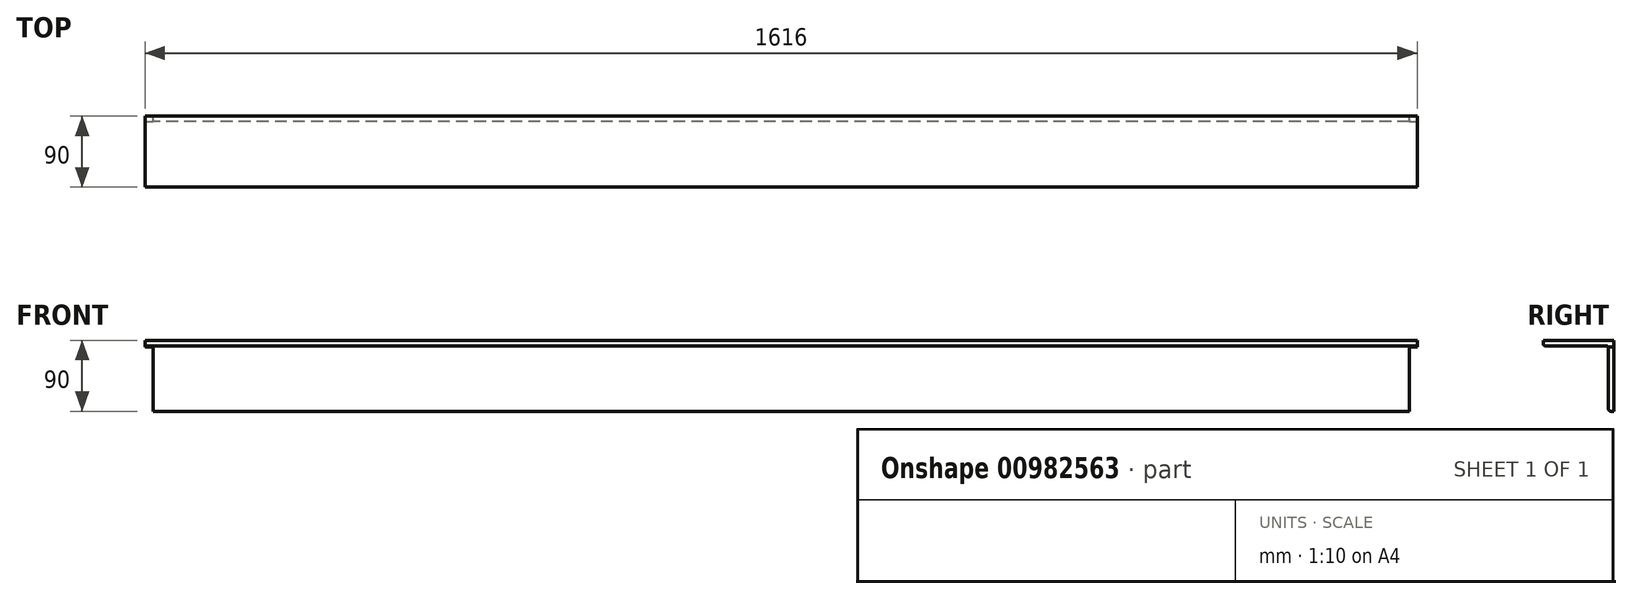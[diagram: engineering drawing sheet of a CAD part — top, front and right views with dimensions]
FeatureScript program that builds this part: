
annotation { "Feature Type Name" : "Feature", "Feature Type Description" : "" }
export const myFeature = defineFeature(function(context is Context, id is Id, definition is map)
    precondition{}
    {
        {
            var Q0;
            Q0=qCreatedBy(makeId("Right.planeOp"),FACE);
            var sketch = newSketch(context, id + "F0", { "sketchPlane" : qUnion([Q0])});
            skLineSegment(sketch, "E0", {"start": v(0, 0) * mm, "end": v(-90, 0) * mm});
            skLineSegment(sketch, "E1", {"start": v(-90, 0) * mm, "end": v(-90, -4) * mm});
            skLineSegment(sketch, "E2", {"start": v(-87, -7) * mm, "end": v(-10, -7) * mm});
            skLineSegment(sketch, "E3", {"start": v(-7, -10) * mm, "end": v(-7, -87) * mm});
            skLineSegment(sketch, "E4", {"start": v(-4, -90) * mm, "end": v(0, -90) * mm});
            skLineSegment(sketch, "E5", {"start": v(0, -90) * mm, "end": v(0, 0) * mm});
            skPoint(sketch, "E6.visualSharp", {"position": v(-90, -7) * mm});
            skArc(sketch, "E6.filletArc", {"start": v(-90, -4) * mm, "mid": v(-89.12, -6.12) * mm, "end": v(-87, -7) * mm});
            skPoint(sketch, "E7.visualSharp", {"position": v(-7, -7) * mm});
            skArc(sketch, "E7.filletArc", {"start": v(-7, -10) * mm, "mid": v(-7.88, -7.88) * mm, "end": v(-10, -7) * mm});
            skPoint(sketch, "E8.visualSharp", {"position": v(-7, -90) * mm});
            skArc(sketch, "E8.filletArc", {"start": v(-7, -87) * mm, "mid": v(-6.12, -89.12) * mm, "end": v(-4, -90) * mm});
            skSolve(sketch);
        }
        {
            var Q0;
            Q0=makeQuery(id+"F0.imprint","IMPRINT",FACE,{"disambiguationData":[TD([[makeQuery(id+"F0.imprint","IMPRINT",EDGE,{"derivedFrom":sQuery(id+"F0.wireOp",EDGE,"E0")}),1.0]])]});
            extrude(context, id + "F1", {"entities" : qUnion([Q0]), "endBound" : BoundingType.SYMMETRIC, "depth" : 1616 * mm, "offsetDistance" : 25 * mm});
        }
        {
            var Q0;
            Q0=makeQuery(id+"F1.opExtrude","SWEPT_FACE",FACE,{"disambiguationData":[OSD([sQuery(id+"F0.wireOp",EDGE,"E5")])]});
            var sketch = newSketch(context, id + "F2", { "sketchPlane" : qUnion([Q0])});
            skLineSegment(sketch, "E9.bottom", {"start": v(-808, -90) * mm, "end": v(-798, -90) * mm});
            skLineSegment(sketch, "E9.top", {"start": v(-808, -8) * mm, "end": v(-798, -8) * mm});
            skLineSegment(sketch, "E9.left", {"start": v(-808, -90) * mm, "end": v(-808, -8) * mm});
            skLineSegment(sketch, "E9.right", {"start": v(-798, -90) * mm, "end": v(-798, -8) * mm});
            skLineSegment(sketch, "E10.MirrorCS", {"start": v(808, -90) * mm, "end": v(798, -90) * mm});
            skLineSegment(sketch, "E11.MirrorCS", {"start": v(808, -8) * mm, "end": v(798, -8) * mm});
            skLineSegment(sketch, "E12.MirrorCS", {"start": v(798, -90) * mm, "end": v(798, -8) * mm});
            skLineSegment(sketch, "E13.MirrorCS", {"start": v(808, -90) * mm, "end": v(808, -8) * mm});
            skSolve(sketch);
        }
        {
            var Q0;
            Q0=makeQuery(id+"F2.imprint","IMPRINT",FACE,{"disambiguationData":[TD([[makeQuery(id+"F2.imprint","IMPRINT",EDGE,{"derivedFrom":sQuery(id+"F2.wireOp",EDGE,"E9.bottom")}),1.0]])]});
            var Q1;
            Q1=makeQuery(id+"F2.imprint","IMPRINT",FACE,{"disambiguationData":[TD([[makeQuery(id+"F2.imprint","IMPRINT",EDGE,{"derivedFrom":sQuery(id+"F2.wireOp",EDGE,"E10.MirrorCS")}),1.0]])]});
            extrude(context, id + "F3", {"entities" : qUnion([Q0, Q1]), "operationType" : NewBodyOperationType.REMOVE, "oppositeDirection" : true, "depth" : 25 * mm, "offsetDistance" : 25 * mm});
        }
    });
